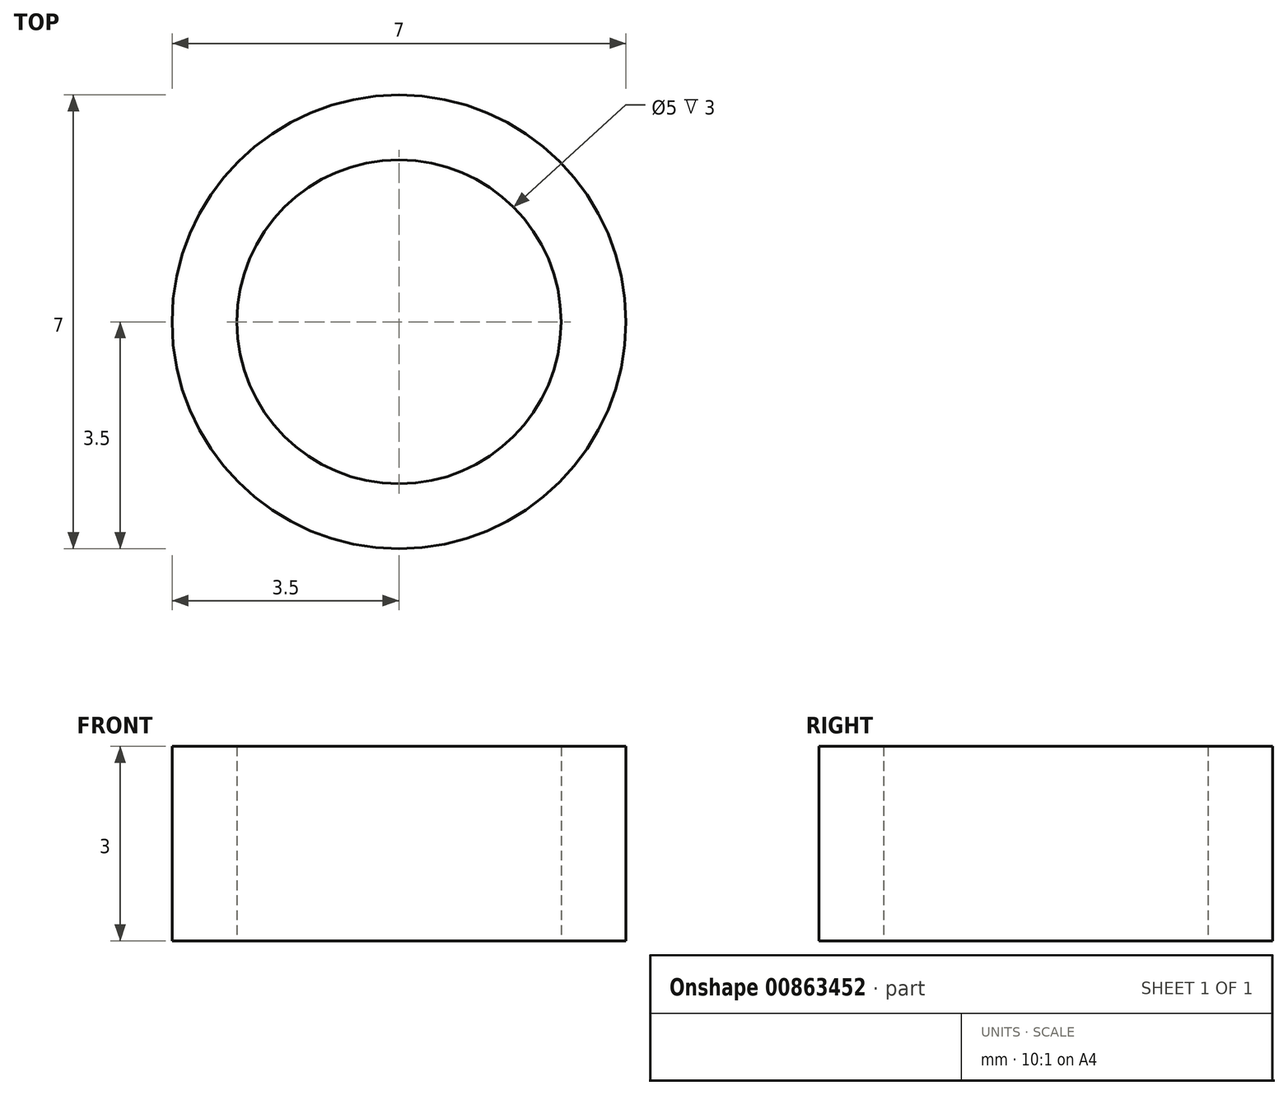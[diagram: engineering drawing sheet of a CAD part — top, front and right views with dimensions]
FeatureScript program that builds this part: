
annotation { "Feature Type Name" : "Feature", "Feature Type Description" : "" }
export const myFeature = defineFeature(function(context is Context, id is Id, definition is map)
    precondition{}
    {
        {
            var Q0;
            Q0=qCreatedBy(makeId("Top.planeOp"),FACE);
            var sketch = newSketch(context, id + "F0", { "sketchPlane" : qUnion([Q0])});
            skCircle(sketch, "E0", {"center": v(0, 0) * mm, "radius": 2.5 * mm});
            skCircle(sketch, "E1", {"center": v(0, 0) * mm, "radius": 3.5 * mm});
            skSolve(sketch);
        }
        {
            var Q0;
            Q0=makeQuery(id+"F0.imprint","IMPRINT",FACE,{"disambiguationData":[TD([[makeQuery(id+"F0.imprint","IMPRINT",EDGE,{"derivedFrom":sQuery(id+"F0.wireOp",EDGE,"E0")}),-1.0]])]});
            extrude(context, id + "F1", {"entities" : qUnion([Q0]), "depth" : 3 * mm, "offsetDistance" : 25 * mm});
        }
    });
